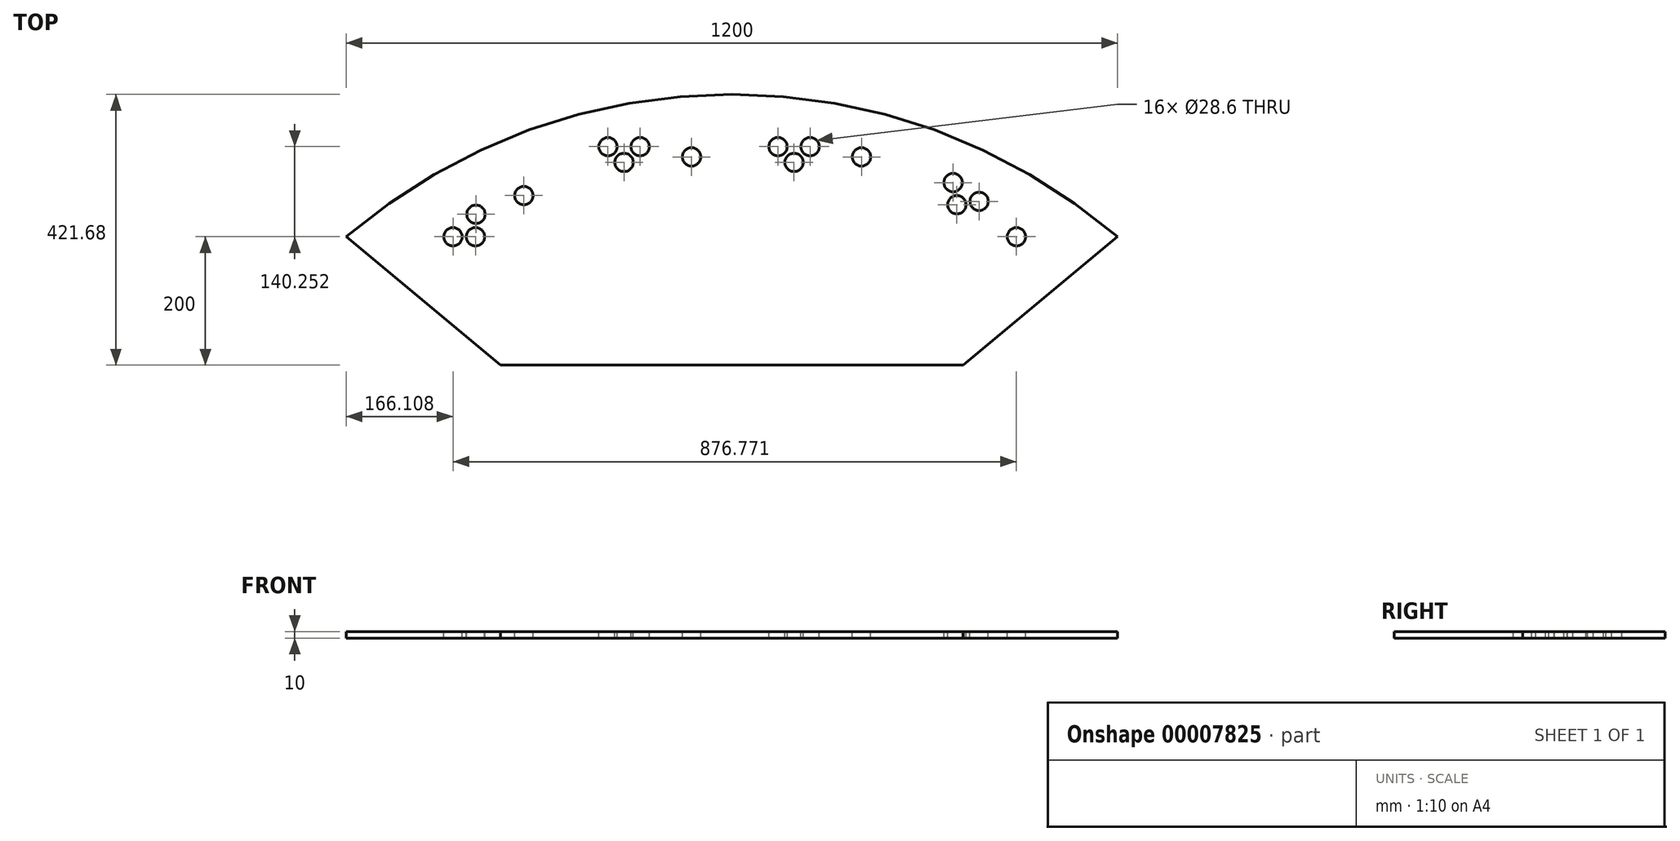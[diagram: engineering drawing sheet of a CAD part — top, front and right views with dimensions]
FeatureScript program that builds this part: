
annotation { "Feature Type Name" : "Feature", "Feature Type Description" : "" }
export const myFeature = defineFeature(function(context is Context, id is Id, definition is map)
    precondition{}
    {
        {
            var Q0;
            Q0=qCreatedBy(makeId("Top.planeOp"),FACE);
            var sketch = newSketch(context, id + "F0", { "sketchPlane" : qUnion([Q0])});
            skArc(sketch, "E0", {"start": v(1200, 0) * mm, "mid": v(600, 221.68) * mm, "end": v(0, 0) * mm});
            skLineSegment(sketch, "E1", {"start": v(240, -200) * mm, "end": v(960, -200) * mm});
            skLineSegment(sketch, "E2", {"start": v(0, 0) * mm, "end": v(240, -200) * mm});
            skLineSegment(sketch, "E3", {"start": v(960, -200) * mm, "end": v(1200, 0) * mm});
            skSolve(sketch);
        }
        {
            var Q0;
            Q0=makeQuery(id+"F0.imprint","IMPRINT",FACE,{"disambiguationData":[TD([[makeQuery(id+"F0.imprint","IMPRINT",EDGE,{"derivedFrom":sQuery(id+"F0.wireOp",EDGE,"E0")}),1.0]])]});
            extrude(context, id + "F1", {"entities" : qUnion([Q0]), "depth" : 10 * mm});
        }
        {
            var Q0;
            Q0=makeQuery(id+"F1.opExtrude","CAP_FACE",FACE,{"disambiguationData":[OSD([sQuery(id+"F0.wireOp",EDGE,"E0"),sQuery(id+"F0.wireOp",EDGE,"E1"),sQuery(id+"F0.wireOp",EDGE,"E2"),sQuery(id+"F0.wireOp",EDGE,"E3")])],"isStart":false});
            var sketch = newSketch(context, id + "F2", { "sketchPlane" : qUnion([Q0])});
            skLineSegment(sketch, "E4", {"start": v(600, -200) * mm, "end": v(280.18, 164.49) * mm, "construction": true});
            skLineSegment(sketch, "E5", {"start": v(600, -200) * mm, "end": v(919.82, 164.49) * mm, "construction": true});
            skLineSegment(sketch, "E6", {"start": v(600, -200) * mm, "end": v(600, 221.68) * mm, "construction": true});
            skLineSegment(sketch, "E7", {"start": v(280.18, 164.49) * mm, "end": v(600, 221.68) * mm, "construction": true});
            skLineSegment(sketch, "E8", {"start": v(280.18, 164.49) * mm, "end": v(0, 0) * mm, "construction": true});
            skLineSegment(sketch, "E9", {"start": v(600, 221.68) * mm, "end": v(919.82, 164.49) * mm, "construction": true});
            skLineSegment(sketch, "E10", {"start": v(919.82, 164.49) * mm, "end": v(1200, 0) * mm, "construction": true});
            skLineSegment(sketch, "E11", {"start": v(1200, 0) * mm, "end": v(600, -200) * mm, "construction": true});
            skLineSegment(sketch, "E12", {"start": v(600.56, -197.12) * mm, "end": v(5.45, 4.63) * mm, "construction": true});
            skCircle(sketch, "E13", {"center": v(801.8, 124.33) * mm, "radius": 14.3 * mm});
            skCircle(sketch, "E14", {"center": v(721.8, 140.25) * mm, "radius": 14.3 * mm});
            skCircle(sketch, "E15", {"center": v(696.8, 115.76) * mm, "radius": 14.3 * mm});
            skCircle(sketch, "E16", {"center": v(671.8, 140.25) * mm, "radius": 14.3 * mm});
            skLineSegment(sketch, "E17", {"start": v(721.8, 140.25) * mm, "end": v(671.8, 140.25) * mm, "construction": true});
            skLineSegment(sketch, "E18", {"start": v(721.8, 140.25) * mm, "end": v(696.8, 115.76) * mm, "construction": true});
            skLineSegment(sketch, "E19", {"start": v(696.8, 115.76) * mm, "end": v(671.8, 140.25) * mm, "construction": true});
            skCircle(sketch, "E20.1.0.0", {"center": v(537.26, 124.33) * mm, "radius": 14.3 * mm});
            skCircle(sketch, "E20.1.0.1", {"center": v(457.26, 140.25) * mm, "radius": 14.3 * mm});
            skCircle(sketch, "E20.1.0.2", {"center": v(432.26, 115.76) * mm, "radius": 14.3 * mm});
            skCircle(sketch, "E20.1.0.3", {"center": v(407.26, 140.25) * mm, "radius": 14.3 * mm});
            skLineSegment(sketch, "E20.1.0.4", {"start": v(457.26, 140.25) * mm, "end": v(432.26, 115.76) * mm, "construction": true});
            skLineSegment(sketch, "E20.1.0.5", {"start": v(457.26, 140.25) * mm, "end": v(407.26, 140.25) * mm, "construction": true});
            skLineSegment(sketch, "E20.1.0.6", {"start": v(432.26, 115.76) * mm, "end": v(407.26, 140.25) * mm, "construction": true});
            skLineSegment(sketch, "E20.direction1", {"start": v(801.8, 124.33) * mm, "end": v(537.26, 124.33) * mm, "construction": true});
            skCircle(sketch, "E21", {"center": v(276.33, 64.13) * mm, "radius": 14.3 * mm});
            skCircle(sketch, "E22", {"center": v(201.82, 35) * mm, "radius": 14.3 * mm});
            skCircle(sketch, "E23", {"center": v(166.1, 0) * mm, "radius": 14.3 * mm});
            skCircle(sketch, "E24", {"center": v(201.1, 0) * mm, "radius": 14.3 * mm});
            skCircle(sketch, "E25", {"center": v(1042.88, 0) * mm, "radius": 14.3 * mm});
            skCircle(sketch, "E26", {"center": v(950.16, 49.82) * mm, "radius": 14.3 * mm});
            skCircle(sketch, "E27", {"center": v(984.78, 55) * mm, "radius": 14.3 * mm});
            skCircle(sketch, "E28", {"center": v(944.28, 84.32) * mm, "radius": 14.3 * mm});
            skLineSegment(sketch, "E29", {"start": v(166.1, 0) * mm, "end": v(201.82, 35) * mm, "construction": true});
            skLineSegment(sketch, "E30", {"start": v(201.82, 35) * mm, "end": v(201.1, 0) * mm, "construction": true});
            skLineSegment(sketch, "E31", {"start": v(201.1, 0) * mm, "end": v(166.1, 0) * mm, "construction": true});
            skLineSegment(sketch, "E32", {"start": v(984.78, 55) * mm, "end": v(944.28, 84.32) * mm, "construction": true});
            skLineSegment(sketch, "E33", {"start": v(944.28, 84.32) * mm, "end": v(950.16, 49.82) * mm, "construction": true});
            skLineSegment(sketch, "E34", {"start": v(984.78, 55) * mm, "end": v(950.16, 49.82) * mm, "construction": true});
            skSolve(sketch);
        }
        {
            var Q0;
            Q0 = qSketchRegion(id + "F2", true);
            extrude(context, id + "F3", {"entities" : qUnion([Q0]), "operationType" : NewBodyOperationType.REMOVE, "endBound" : BoundingType.THROUGH_ALL, "oppositeDirection" : true, "depth" : 25 * mm});
        }
    });
